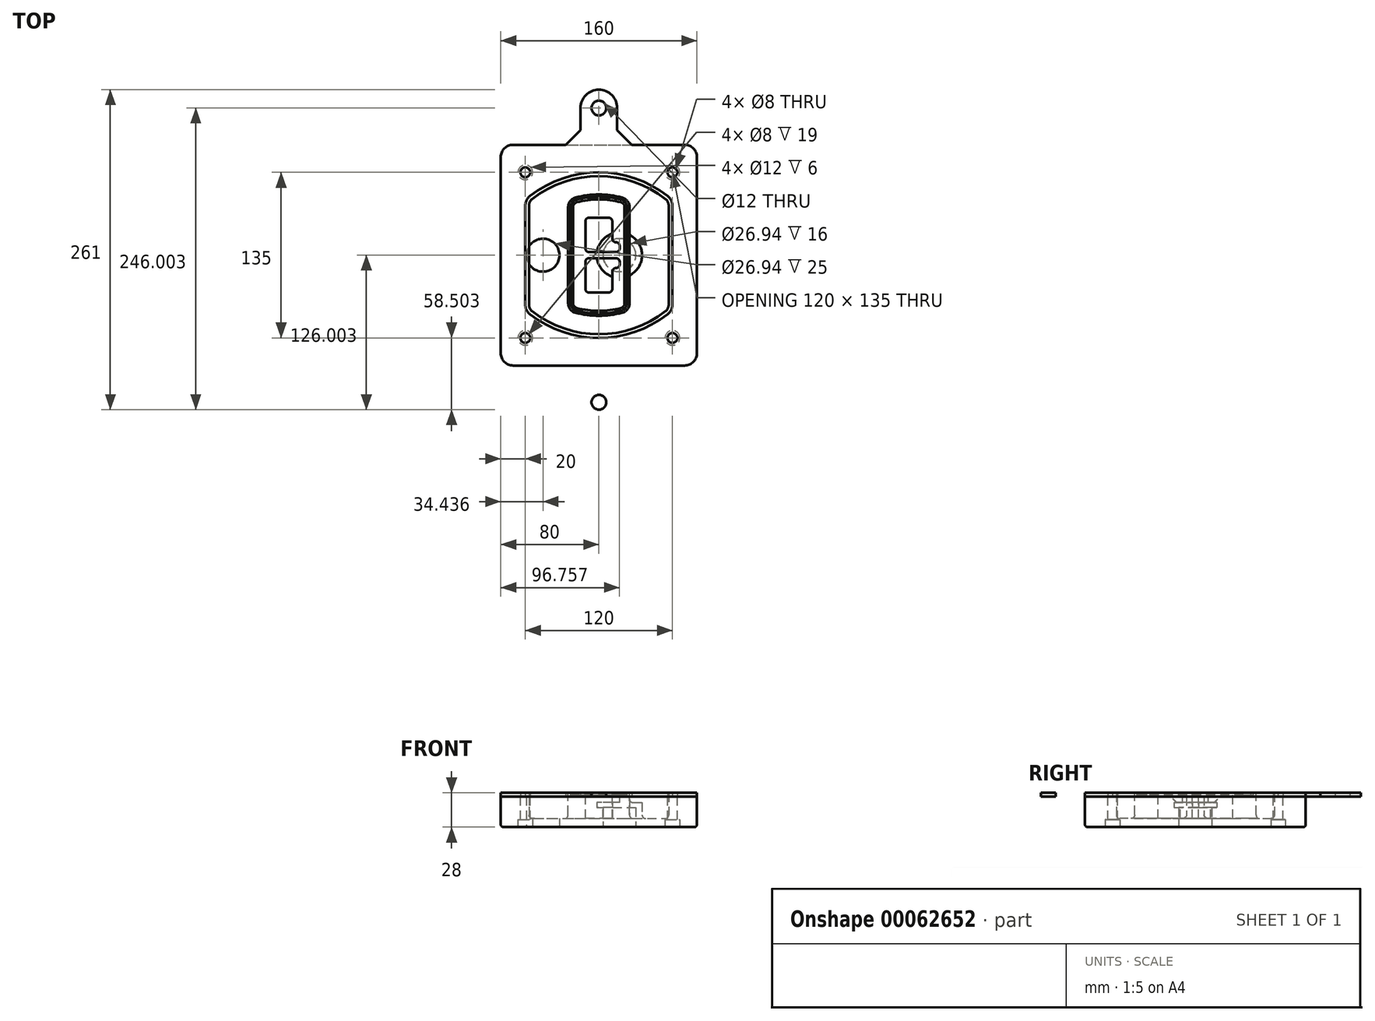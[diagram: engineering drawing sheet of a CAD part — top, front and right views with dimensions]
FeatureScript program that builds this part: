
annotation { "Feature Type Name" : "Feature", "Feature Type Description" : "" }
export const myFeature = defineFeature(function(context is Context, id is Id, definition is map)
    precondition{}
    {
        {
            var Q0;
            Q0=qCreatedBy(makeId("Top.planeOp"),FACE);
            var sketch = newSketch(context, id + "F0", { "sketchPlane" : qUnion([Q0])});
            skPoint(sketch, "E0.rect.middle", {"position": v(0, 0) * mm});
            skLineSegment(sketch, "E1.bottom", {"start": v(24.05, 28.38) * mm, "end": v(164.05, 28.38) * mm});
            skLineSegment(sketch, "E1.top", {"start": v(24.05, 208.38) * mm, "end": v(164.05, 208.38) * mm});
            skLineSegment(sketch, "E1.left", {"start": v(14.05, 38.38) * mm, "end": v(14.05, 198.38) * mm});
            skLineSegment(sketch, "E1.right", {"start": v(174.05, 38.38) * mm, "end": v(174.05, 198.38) * mm});
            skLineSegment(sketch, "E2", {"start": v(14.05, 208.38) * mm, "end": v(174.05, 28.38) * mm, "construction": true});
            skLineSegment(sketch, "E3", {"start": v(174.05, 208.38) * mm, "end": v(14.05, 28.38) * mm, "construction": true});
            skCircle(sketch, "E4", {"center": v(34.05, 185.88) * mm, "radius": 4 * mm});
            skCircle(sketch, "E5", {"center": v(154.05, 185.88) * mm, "radius": 4 * mm});
            skCircle(sketch, "E6", {"center": v(154.05, 50.88) * mm, "radius": 4 * mm});
            skCircle(sketch, "E7", {"center": v(34.05, 50.88) * mm, "radius": 4 * mm});
            skLineSegment(sketch, "E8", {"start": v(34.05, 185.88) * mm, "end": v(154.05, 185.88) * mm, "construction": true});
            skLineSegment(sketch, "E9", {"start": v(154.05, 185.88) * mm, "end": v(154.05, 50.88) * mm, "construction": true});
            skLineSegment(sketch, "E10", {"start": v(154.05, 50.88) * mm, "end": v(34.05, 50.88) * mm, "construction": true});
            skLineSegment(sketch, "E11", {"start": v(34.05, 50.88) * mm, "end": v(34.05, 185.88) * mm, "construction": true});
            skLineSegment(sketch, "E12", {"start": v(34.05, 158.68) * mm, "end": v(34.05, 78.09) * mm});
            skLineSegment(sketch, "E13", {"start": v(154.05, 158.68) * mm, "end": v(154.05, 78.09) * mm});
            skArc(sketch, "E14", {"start": v(150.2, 166.56) * mm, "mid": v(94.05, 185.88) * mm, "end": v(37.9, 166.56) * mm});
            skArc(sketch, "E15", {"start": v(37.9, 70.2) * mm, "mid": v(94.05, 50.88) * mm, "end": v(150.2, 70.2) * mm});
            skLineSegment(sketch, "E16", {"start": v(34.05, 118.38) * mm, "end": v(154.05, 118.38) * mm, "construction": true});
            skPoint(sketch, "E17.visualSharp", {"position": v(34.05, 73.38) * mm});
            skArc(sketch, "E17.filletArc", {"start": v(34.05, 78.09) * mm, "mid": v(35.06, 73.7) * mm, "end": v(37.9, 70.2) * mm});
            skPoint(sketch, "E18.visualSharp", {"position": v(34.05, 163.38) * mm});
            skArc(sketch, "E18.filletArc", {"start": v(37.9, 166.56) * mm, "mid": v(35.06, 163.06) * mm, "end": v(34.05, 158.68) * mm});
            skPoint(sketch, "E19.visualSharp", {"position": v(154.05, 163.38) * mm});
            skArc(sketch, "E19.filletArc", {"start": v(154.05, 158.68) * mm, "mid": v(153.04, 163.06) * mm, "end": v(150.2, 166.56) * mm});
            skPoint(sketch, "E20.visualSharp", {"position": v(154.05, 73.38) * mm});
            skArc(sketch, "E20.filletArc", {"start": v(150.2, 70.2) * mm, "mid": v(153.04, 73.7) * mm, "end": v(154.05, 78.09) * mm});
            skPoint(sketch, "E21.visualSharp", {"position": v(14.05, 208.38) * mm});
            skArc(sketch, "E21.filletArc", {"start": v(24.05, 208.38) * mm, "mid": v(16.98, 205.45) * mm, "end": v(14.05, 198.38) * mm});
            skPoint(sketch, "E22.visualSharp", {"position": v(174.05, 208.38) * mm});
            skArc(sketch, "E22.filletArc", {"start": v(174.05, 198.38) * mm, "mid": v(171.12, 205.45) * mm, "end": v(164.05, 208.38) * mm});
            skPoint(sketch, "E23.visualSharp", {"position": v(174.05, 28.38) * mm});
            skArc(sketch, "E23.filletArc", {"start": v(164.05, 28.38) * mm, "mid": v(171.12, 31.31) * mm, "end": v(174.05, 38.38) * mm});
            skPoint(sketch, "E24.visualSharp", {"position": v(14.05, 28.38) * mm});
            skArc(sketch, "E24.filletArc", {"start": v(14.05, 38.38) * mm, "mid": v(16.98, 31.31) * mm, "end": v(24.05, 28.38) * mm});
            skArc(sketch, "E25.0", {"start": v(151.05, 158.68) * mm, "mid": v(150.34, 161.75) * mm, "end": v(148.36, 164.2) * mm});
            skLineSegment(sketch, "E25.1", {"start": v(151.05, 158.68) * mm, "end": v(151.05, 78.09) * mm});
            skArc(sketch, "E25.2", {"start": v(148.36, 72.57) * mm, "mid": v(150.34, 75.02) * mm, "end": v(151.05, 78.09) * mm});
            skArc(sketch, "E25.3", {"start": v(39.74, 72.57) * mm, "mid": v(94.05, 53.88) * mm, "end": v(148.36, 72.57) * mm});
            skArc(sketch, "E25.4", {"start": v(37.05, 78.09) * mm, "mid": v(37.76, 75.02) * mm, "end": v(39.74, 72.57) * mm});
            skArc(sketch, "E25.5", {"start": v(148.36, 164.2) * mm, "mid": v(94.05, 182.88) * mm, "end": v(39.74, 164.2) * mm});
            skLineSegment(sketch, "E25.6", {"start": v(37.05, 158.68) * mm, "end": v(37.05, 78.09) * mm});
            skArc(sketch, "E25.7", {"start": v(39.74, 164.2) * mm, "mid": v(37.76, 161.75) * mm, "end": v(37.05, 158.68) * mm});
            skArc(sketch, "E26.0", {"start": v(35.43, 169.71) * mm, "mid": v(31.47, 164.82) * mm, "end": v(30.05, 158.68) * mm});
            skArc(sketch, "E26.1", {"start": v(152.67, 169.71) * mm, "mid": v(94.05, 189.88) * mm, "end": v(35.43, 169.71) * mm});
            skArc(sketch, "E26.2", {"start": v(158.05, 158.68) * mm, "mid": v(156.63, 164.82) * mm, "end": v(152.67, 169.71) * mm});
            skLineSegment(sketch, "E26.3", {"start": v(158.05, 158.68) * mm, "end": v(158.05, 78.09) * mm});
            skArc(sketch, "E26.4", {"start": v(152.67, 67.05) * mm, "mid": v(156.63, 71.95) * mm, "end": v(158.05, 78.09) * mm});
            skLineSegment(sketch, "E26.5", {"start": v(30.05, 158.68) * mm, "end": v(30.05, 78.09) * mm});
            skArc(sketch, "E26.6", {"start": v(35.43, 67.05) * mm, "mid": v(94.05, 46.88) * mm, "end": v(152.67, 67.05) * mm});
            skArc(sketch, "E26.7", {"start": v(30.05, 78.09) * mm, "mid": v(31.47, 71.95) * mm, "end": v(35.43, 67.05) * mm});
            skSolve(sketch);
        }
        {
            var Q0;
            Q0=makeQuery(id+"F0.imprint","IMPRINT",FACE,{"disambiguationData":[TD([[makeQuery(id+"F0.imprint","IMPRINT",EDGE,{"derivedFrom":sQuery(id+"F0.wireOp",EDGE,"E1.bottom")}),1.0]])]});
            var Q1;
            Q1=makeQuery(id+"F0.imprint","IMPRINT",FACE,{"disambiguationData":[TD([[makeQuery(id+"F0.imprint","IMPRINT",EDGE,{"derivedFrom":sQuery(id+"F0.wireOp",EDGE,"E12")}),1.0]])]});
            var Q2;
            Q2=makeQuery(id+"F0.imprint","IMPRINT",FACE,{"disambiguationData":[TD([[makeQuery(id+"F0.imprint","IMPRINT",EDGE,{"derivedFrom":sQuery(id+"F0.wireOp",EDGE,"E25.0")}),1.0]])]});
            var Q3;
            Q3=makeQuery(id+"F0.imprint","IMPRINT",FACE,{"disambiguationData":[TD([[makeQuery(id+"F0.imprint","IMPRINT",EDGE,{"derivedFrom":sQuery(id+"F0.wireOp",EDGE,"E12")}),-1.0]])]});
            extrude(context, id + "F1", {"entities" : qUnion([Q0, Q1, Q2, Q3]), "oppositeDirection" : true, "depth" : 25 * mm});
        }
        {
            var Q0;
            Q0=makeQuery(id+"F0.imprint","IMPRINT",FACE,{"disambiguationData":[TD([[makeQuery(id+"F0.imprint","IMPRINT",EDGE,{"derivedFrom":sQuery(id+"F0.wireOp",EDGE,"E12")}),1.0]])]});
            extrude(context, id + "F2", {"entities" : qUnion([Q0]), "operationType" : NewBodyOperationType.ADD, "depth" : 3 * mm});
        }
        {
            var Q0;
            Q0=makeQuery(id+"F0.imprint","IMPRINT",FACE,{"disambiguationData":[TD([[makeQuery(id+"F0.imprint","IMPRINT",EDGE,{"derivedFrom":sQuery(id+"F0.wireOp",EDGE,"E25.0")}),1.0]])]});
            extrude(context, id + "F3", {"entities" : qUnion([Q0]), "operationType" : NewBodyOperationType.REMOVE, "oppositeDirection" : true, "depth" : 18 * mm});
        }
        {
            var Q0;
            Q0=makeQuery(id+"F2.opExtrude","CAP_FACE",FACE,{"disambiguationData":[OSD([sQuery(id+"F0.wireOp",EDGE,"E12"),sQuery(id+"F0.wireOp",EDGE,"E13"),sQuery(id+"F0.wireOp",EDGE,"E14"),sQuery(id+"F0.wireOp",EDGE,"E15"),sQuery(id+"F0.wireOp",EDGE,"E17.filletArc"),sQuery(id+"F0.wireOp",EDGE,"E18.filletArc"),sQuery(id+"F0.wireOp",EDGE,"E19.filletArc"),sQuery(id+"F0.wireOp",EDGE,"E20.filletArc"),sQuery(id+"F0.wireOp",EDGE,"E25.0"),sQuery(id+"F0.wireOp",EDGE,"E25.1"),sQuery(id+"F0.wireOp",EDGE,"E25.2"),sQuery(id+"F0.wireOp",EDGE,"E25.3"),sQuery(id+"F0.wireOp",EDGE,"E25.4"),sQuery(id+"F0.wireOp",EDGE,"E25.5"),sQuery(id+"F0.wireOp",EDGE,"E25.6"),sQuery(id+"F0.wireOp",EDGE,"E25.7")])],"isStart":false});
            var sketch = newSketch(context, id + "F4", { "sketchPlane" : qUnion([Q0])});
            skArc(sketch, "E27.0", {"start": v(74.97, 71.41) * mm, "mid": v(94.05, 68.88) * mm, "end": v(113.13, 71.41) * mm});
            skArc(sketch, "E28.0", {"start": v(113.13, 165.35) * mm, "mid": v(94.05, 167.88) * mm, "end": v(74.97, 165.35) * mm});
            skLineSegment(sketch, "E29", {"start": v(69.05, 157.63) * mm, "end": v(69.05, 79.14) * mm});
            skLineSegment(sketch, "E30", {"start": v(119.05, 157.63) * mm, "end": v(119.05, 79.14) * mm});
            skLineSegment(sketch, "E31", {"start": v(69.05, 163.48) * mm, "end": v(119.05, 163.48) * mm, "construction": true});
            skLineSegment(sketch, "E32", {"start": v(69.05, 73.28) * mm, "end": v(119.05, 73.28) * mm, "construction": true});
            skPoint(sketch, "E33.visualSharp", {"position": v(69.05, 163.48) * mm});
            skArc(sketch, "E33.filletArc", {"start": v(74.97, 165.35) * mm, "mid": v(70.7, 162.5) * mm, "end": v(69.05, 157.63) * mm});
            skPoint(sketch, "E34.visualSharp", {"position": v(119.05, 163.48) * mm});
            skArc(sketch, "E34.filletArc", {"start": v(119.05, 157.63) * mm, "mid": v(117.4, 162.5) * mm, "end": v(113.13, 165.35) * mm});
            skPoint(sketch, "E35.visualSharp", {"position": v(119.05, 73.28) * mm});
            skArc(sketch, "E35.filletArc", {"start": v(113.13, 71.41) * mm, "mid": v(117.4, 74.27) * mm, "end": v(119.05, 79.14) * mm});
            skPoint(sketch, "E36.visualSharp", {"position": v(69.05, 73.28) * mm});
            skArc(sketch, "E36.filletArc", {"start": v(69.05, 79.14) * mm, "mid": v(70.7, 74.27) * mm, "end": v(74.97, 71.41) * mm});
            skArc(sketch, "E37.0", {"start": v(148.36, 164.2) * mm, "mid": v(94.05, 182.88) * mm, "end": v(39.74, 164.2) * mm});
            skArc(sketch, "E37.1", {"start": v(39.74, 164.2) * mm, "mid": v(37.76, 161.75) * mm, "end": v(37.05, 158.68) * mm});
            skLineSegment(sketch, "E37.2", {"start": v(37.05, 158.68) * mm, "end": v(37.05, 78.09) * mm});
            skArc(sketch, "E37.3", {"start": v(37.05, 78.09) * mm, "mid": v(37.76, 75.02) * mm, "end": v(39.74, 72.57) * mm});
            skArc(sketch, "E37.4", {"start": v(39.74, 72.57) * mm, "mid": v(94.05, 53.88) * mm, "end": v(148.36, 72.57) * mm});
            skArc(sketch, "E37.5", {"start": v(148.36, 72.57) * mm, "mid": v(150.34, 75.02) * mm, "end": v(151.05, 78.09) * mm});
            skLineSegment(sketch, "E37.6", {"start": v(151.05, 158.68) * mm, "end": v(151.05, 78.09) * mm});
            skArc(sketch, "E37.7", {"start": v(151.05, 158.68) * mm, "mid": v(150.34, 161.75) * mm, "end": v(148.36, 164.2) * mm});
            skLineSegment(sketch, "E38.0", {"start": v(117.05, 157.63) * mm, "end": v(117.05, 79.14) * mm});
            skArc(sketch, "E38.1", {"start": v(112.61, 73.34) * mm, "mid": v(115.81, 75.49) * mm, "end": v(117.05, 79.14) * mm});
            skArc(sketch, "E38.2", {"start": v(75.49, 73.34) * mm, "mid": v(94.05, 70.88) * mm, "end": v(112.61, 73.34) * mm});
            skArc(sketch, "E38.3", {"start": v(71.05, 79.14) * mm, "mid": v(72.29, 75.49) * mm, "end": v(75.49, 73.34) * mm});
            skLineSegment(sketch, "E38.4", {"start": v(71.05, 157.63) * mm, "end": v(71.05, 79.14) * mm});
            skArc(sketch, "E38.5", {"start": v(117.05, 157.63) * mm, "mid": v(115.81, 161.28) * mm, "end": v(112.61, 163.42) * mm});
            skArc(sketch, "E38.6", {"start": v(75.49, 163.42) * mm, "mid": v(72.29, 161.28) * mm, "end": v(71.05, 157.63) * mm});
            skArc(sketch, "E38.7", {"start": v(112.61, 163.42) * mm, "mid": v(94.05, 165.88) * mm, "end": v(75.49, 163.42) * mm});
            skArc(sketch, "E39.0", {"start": v(115.05, 157.63) * mm, "mid": v(114.23, 160.06) * mm, "end": v(112.1, 161.5) * mm});
            skLineSegment(sketch, "E39.1", {"start": v(115.05, 157.63) * mm, "end": v(115.05, 79.14) * mm});
            skArc(sketch, "E39.2", {"start": v(112.1, 75.27) * mm, "mid": v(114.23, 76.7) * mm, "end": v(115.05, 79.14) * mm});
            skArc(sketch, "E39.3", {"start": v(76, 75.27) * mm, "mid": v(94.05, 72.88) * mm, "end": v(112.1, 75.27) * mm});
            skArc(sketch, "E39.4", {"start": v(73.05, 79.14) * mm, "mid": v(73.87, 76.7) * mm, "end": v(76, 75.27) * mm});
            skArc(sketch, "E39.5", {"start": v(112.1, 161.5) * mm, "mid": v(94.05, 163.88) * mm, "end": v(76, 161.5) * mm});
            skLineSegment(sketch, "E39.6", {"start": v(73.05, 157.63) * mm, "end": v(73.05, 79.14) * mm});
            skArc(sketch, "E39.7", {"start": v(76, 161.5) * mm, "mid": v(73.87, 160.06) * mm, "end": v(73.05, 157.63) * mm});
            skLineSegment(sketch, "E40", {"start": v(69.05, 118.38) * mm, "end": v(119.05, 118.38) * mm, "construction": true});
            skLineSegment(sketch, "E41", {"start": v(83.05, 123.88) * mm, "end": v(83.05, 145.88) * mm});
            skLineSegment(sketch, "E42", {"start": v(86.05, 148.88) * mm, "end": v(102.05, 148.88) * mm});
            skLineSegment(sketch, "E43", {"start": v(105.05, 145.88) * mm, "end": v(105.05, 131.88) * mm});
            skLineSegment(sketch, "E44", {"start": v(108.05, 128.88) * mm, "end": v(108.05, 128.88) * mm});
            skLineSegment(sketch, "E45", {"start": v(111.05, 125.88) * mm, "end": v(111.05, 123.88) * mm});
            skLineSegment(sketch, "E46", {"start": v(108.05, 120.88) * mm, "end": v(86.05, 120.88) * mm});
            skPoint(sketch, "E47.visualSharp", {"position": v(83.05, 148.88) * mm});
            skArc(sketch, "E47.filletArc", {"start": v(86.05, 148.88) * mm, "mid": v(83.93, 148) * mm, "end": v(83.05, 145.88) * mm});
            skPoint(sketch, "E48.visualSharp", {"position": v(105.05, 148.88) * mm});
            skArc(sketch, "E48.filletArc", {"start": v(105.05, 145.88) * mm, "mid": v(104.17, 148) * mm, "end": v(102.05, 148.88) * mm});
            skPoint(sketch, "E49.visualSharp", {"position": v(105.05, 128.88) * mm});
            skArc(sketch, "E49.filletArc", {"start": v(105.05, 131.88) * mm, "mid": v(105.93, 129.76) * mm, "end": v(108.05, 128.88) * mm});
            skPoint(sketch, "E50.visualSharp", {"position": v(111.05, 128.88) * mm});
            skArc(sketch, "E50.filletArc", {"start": v(111.05, 125.88) * mm, "mid": v(110.17, 128) * mm, "end": v(108.05, 128.88) * mm});
            skPoint(sketch, "E51.visualSharp", {"position": v(111.05, 120.88) * mm});
            skArc(sketch, "E51.filletArc", {"start": v(108.05, 120.88) * mm, "mid": v(110.17, 121.76) * mm, "end": v(111.05, 123.88) * mm});
            skPoint(sketch, "E52.visualSharp", {"position": v(83.05, 120.88) * mm});
            skArc(sketch, "E52.filletArc", {"start": v(83.05, 123.88) * mm, "mid": v(83.93, 121.76) * mm, "end": v(86.05, 120.88) * mm});
            skLineSegment(sketch, "E53.0.MirrorCS", {"start": v(108.05, 115.88) * mm, "end": v(86.05, 115.88) * mm});
            skArc(sketch, "E54.0.MirrorCS", {"start": v(83.05, 112.88) * mm, "mid": v(83.93, 115) * mm, "end": v(86.05, 115.88) * mm});
            skLineSegment(sketch, "E55.0.MirrorCS", {"start": v(83.05, 112.88) * mm, "end": v(83.05, 90.88) * mm});
            skArc(sketch, "E56.0.MirrorCS", {"start": v(86.05, 87.88) * mm, "mid": v(83.93, 88.76) * mm, "end": v(83.05, 90.88) * mm});
            skLineSegment(sketch, "E57.0.MirrorCS", {"start": v(86.05, 87.88) * mm, "end": v(102.05, 87.88) * mm});
            skArc(sketch, "E58.0.MirrorCS", {"start": v(105.05, 90.88) * mm, "mid": v(104.17, 88.76) * mm, "end": v(102.05, 87.88) * mm});
            skLineSegment(sketch, "E59.0.MirrorCS", {"start": v(105.05, 90.88) * mm, "end": v(105.05, 104.88) * mm});
            skArc(sketch, "E60.0.MirrorCS", {"start": v(105.05, 104.88) * mm, "mid": v(105.93, 107) * mm, "end": v(108.05, 107.88) * mm});
            skArc(sketch, "E61.0.MirrorCS", {"start": v(111.05, 110.88) * mm, "mid": v(110.17, 108.76) * mm, "end": v(108.05, 107.88) * mm});
            skLineSegment(sketch, "E62.0.MirrorCS", {"start": v(111.05, 110.88) * mm, "end": v(111.05, 112.88) * mm});
            skArc(sketch, "E63.0.MirrorCS", {"start": v(108.05, 115.88) * mm, "mid": v(110.17, 115) * mm, "end": v(111.05, 112.88) * mm});
            skSolve(sketch);
        }
        {
            var Q0;
            Q0=makeQuery(id+"F4.imprint","IMPRINT",FACE,{"disambiguationData":[TD([[makeQuery(id+"F4.imprint","IMPRINT",EDGE,{"derivedFrom":sQuery(id+"F4.wireOp",EDGE,"E27.0")}),1.0]])]});
            var Q1;
            Q1=makeQuery(id+"F4.imprint","IMPRINT",FACE,{"disambiguationData":[TD([[makeQuery(id+"F4.imprint","IMPRINT",EDGE,{"derivedFrom":sQuery(id+"F4.wireOp",EDGE,"E38.0")}),-1.0]])]});
            var Q2;
            Q2=makeQuery(id+"F4.imprint","IMPRINT",FACE,{"disambiguationData":[TD([[makeQuery(id+"F4.imprint","IMPRINT",EDGE,{"derivedFrom":sQuery(id+"F4.wireOp",EDGE,"E39.0")}),1.0]])]});
            extrude(context, id + "F5", {"entities" : qUnion([Q0, Q1, Q2]), "operationType" : NewBodyOperationType.ADD, "endBound" : BoundingType.UP_TO_NEXT, "oppositeDirection" : true, "depth" : 25 * mm});
        }
        {
            var Q0;
            Q0=makeQuery(id+"F4.imprint","IMPRINT",FACE,{"disambiguationData":[TD([[makeQuery(id+"F4.imprint","IMPRINT",EDGE,{"derivedFrom":sQuery(id+"F4.wireOp",EDGE,"E38.0")}),-1.0]])]});
            extrude(context, id + "F6", {"entities" : qUnion([Q0]), "operationType" : NewBodyOperationType.REMOVE, "oppositeDirection" : true, "depth" : 2 * mm});
        }
        {
            var Q0;
            Q0=makeQuery(id+"F1.opExtrude","CAP_FACE",FACE,{"disambiguationData":[OSD([sQuery(id+"F0.wireOp",EDGE,"E1.bottom"),sQuery(id+"F0.wireOp",EDGE,"E1.top"),sQuery(id+"F0.wireOp",EDGE,"E1.left"),sQuery(id+"F0.wireOp",EDGE,"E1.right"),sQuery(id+"F0.wireOp",EDGE,"E4"),sQuery(id+"F0.wireOp",EDGE,"E5"),sQuery(id+"F0.wireOp",EDGE,"E6"),sQuery(id+"F0.wireOp",EDGE,"E7"),sQuery(id+"F0.wireOp",EDGE,"E21.filletArc"),sQuery(id+"F0.wireOp",EDGE,"E22.filletArc"),sQuery(id+"F0.wireOp",EDGE,"E23.filletArc"),sQuery(id+"F0.wireOp",EDGE,"E24.filletArc")])],"isStart":false});
            var sketch = newSketch(context, id + "F7", { "sketchPlane" : qUnion([Q0])});
            skCircle(sketch, "E64", {"center": v(110.8, -118.38) * mm, "radius": 13.47 * mm});
            skCircle(sketch, "E65", {"center": v(48.49, -118.38) * mm, "radius": 13.47 * mm});
            skLineSegment(sketch, "E66", {"start": v(174.05, -118.38) * mm, "end": v(14.05, -118.38) * mm});
            skCircle(sketch, "E67", {"center": v(110.8, -118.38) * mm, "radius": 18.47 * mm});
            skCircle(sketch, "E68", {"center": v(154.05, -185.88) * mm, "radius": 6 * mm});
            skCircle(sketch, "E69", {"center": v(34.05, -185.88) * mm, "radius": 6 * mm});
            skCircle(sketch, "E70", {"center": v(34.05, -50.88) * mm, "radius": 6 * mm});
            skCircle(sketch, "E71", {"center": v(154.05, -50.88) * mm, "radius": 6 * mm});
            skSolve(sketch);
        }
        {
            var Q0;
            {var subQ1=sQuery(id+"F7.wireOp",EDGE,"E66");var subQ4=sQuery(id+"F7.wireOp",EDGE,"E64");var subQ6=makeQuery(id+"F7.imprint","INTERSECT",VERTEX,{"disambiguationData":[OD(0.0)],"derivedFrom":[subQ4,subQ1]});Q0=makeQuery(id+"F7.imprint","IMPRINT",FACE,{"disambiguationData":[TD([[makeQuery(id+"F7.imprint","IMPRINT",EDGE,{"disambiguationData":[TD([[subQ6,-1.0]])],"derivedFrom":subQ4}),-1.0]])]});}
            var Q1;
            {var subQ0=sQuery(id+"F7.wireOp",EDGE,"E66");var subQ1=sQuery(id+"F7.wireOp",EDGE,"E64");var subQ3=makeQuery(id+"F7.imprint","INTERSECT",VERTEX,{"disambiguationData":[OD(0.0)],"derivedFrom":[subQ1,subQ0]});Q1=makeQuery(id+"F7.imprint","IMPRINT",FACE,{"disambiguationData":[TD([[makeQuery(id+"F7.imprint","IMPRINT",EDGE,{"disambiguationData":[TD([[subQ3,-1.0]])],"derivedFrom":subQ1}),1.0]])]});}
            var Q2;
            {var subQ0=sQuery(id+"F7.wireOp",EDGE,"E66");var subQ1=sQuery(id+"F7.wireOp",EDGE,"E64");var subQ3=makeQuery(id+"F7.imprint","INTERSECT",VERTEX,{"disambiguationData":[OD(0.0)],"derivedFrom":[subQ1,subQ0]});Q2=makeQuery(id+"F7.imprint","IMPRINT",FACE,{"disambiguationData":[TD([[makeQuery(id+"F7.imprint","IMPRINT",EDGE,{"disambiguationData":[TD([[subQ3,1.0]])],"derivedFrom":subQ1}),1.0]])]});}
            var Q3;
            {var subQ1=sQuery(id+"F7.wireOp",EDGE,"E66");var subQ4=sQuery(id+"F7.wireOp",EDGE,"E64");var subQ6=makeQuery(id+"F7.imprint","INTERSECT",VERTEX,{"disambiguationData":[OD(0.0)],"derivedFrom":[subQ4,subQ1]});Q3=makeQuery(id+"F7.imprint","IMPRINT",FACE,{"disambiguationData":[TD([[makeQuery(id+"F7.imprint","IMPRINT",EDGE,{"disambiguationData":[TD([[subQ6,1.0]])],"derivedFrom":subQ4}),-1.0]])]});}
            extrude(context, id + "F8", {"entities" : qUnion([Q0, Q1, Q2, Q3]), "operationType" : NewBodyOperationType.ADD, "oppositeDirection" : true, "depth" : 20 * mm});
        }
        {
            var Q0;
            {var subQ0=sQuery(id+"F7.wireOp",EDGE,"E66");var subQ1=sQuery(id+"F7.wireOp",EDGE,"E64");var subQ3=makeQuery(id+"F7.imprint","INTERSECT",VERTEX,{"disambiguationData":[OD(0.0)],"derivedFrom":[subQ1,subQ0]});Q0=makeQuery(id+"F7.imprint","IMPRINT",FACE,{"disambiguationData":[TD([[makeQuery(id+"F7.imprint","IMPRINT",EDGE,{"disambiguationData":[TD([[subQ3,-1.0]])],"derivedFrom":subQ1}),1.0]])]});}
            var Q1;
            {var subQ0=sQuery(id+"F7.wireOp",EDGE,"E66");var subQ1=sQuery(id+"F7.wireOp",EDGE,"E64");var subQ3=makeQuery(id+"F7.imprint","INTERSECT",VERTEX,{"disambiguationData":[OD(0.0)],"derivedFrom":[subQ1,subQ0]});Q1=makeQuery(id+"F7.imprint","IMPRINT",FACE,{"disambiguationData":[TD([[makeQuery(id+"F7.imprint","IMPRINT",EDGE,{"disambiguationData":[TD([[subQ3,1.0]])],"derivedFrom":subQ1}),1.0]])]});}
            extrude(context, id + "F9", {"entities" : qUnion([Q0, Q1]), "operationType" : NewBodyOperationType.REMOVE, "oppositeDirection" : true, "depth" : 16 * mm});
        }
        {
            var Q0;
            {var subQ0=sQuery(id+"F7.wireOp",EDGE,"E66");var subQ1=sQuery(id+"F7.wireOp",EDGE,"E65");var subQ3=makeQuery(id+"F7.imprint","INTERSECT",VERTEX,{"disambiguationData":[OD(0.0)],"derivedFrom":[subQ1,subQ0]});Q0=makeQuery(id+"F7.imprint","IMPRINT",FACE,{"disambiguationData":[TD([[makeQuery(id+"F7.imprint","IMPRINT",EDGE,{"disambiguationData":[TD([[subQ3,-1.0]])],"derivedFrom":subQ1}),1.0]])]});}
            var Q1;
            {var subQ0=sQuery(id+"F7.wireOp",EDGE,"E66");var subQ1=sQuery(id+"F7.wireOp",EDGE,"E65");var subQ3=makeQuery(id+"F7.imprint","INTERSECT",VERTEX,{"disambiguationData":[OD(0.0)],"derivedFrom":[subQ1,subQ0]});Q1=makeQuery(id+"F7.imprint","IMPRINT",FACE,{"disambiguationData":[TD([[makeQuery(id+"F7.imprint","IMPRINT",EDGE,{"disambiguationData":[TD([[subQ3,1.0]])],"derivedFrom":subQ1}),1.0]])]});}
            extrude(context, id + "F10", {"entities" : qUnion([Q0, Q1]), "operationType" : NewBodyOperationType.REMOVE, "oppositeDirection" : true, "depth" : 25 * mm});
        }
        {
            var Q0;
            Q0=makeQuery(id+"F7.imprint","IMPRINT",FACE,{"disambiguationData":[TD([[makeQuery(id+"F7.imprint","IMPRINT",EDGE,{"derivedFrom":sQuery(id+"F7.wireOp",EDGE,"E68")}),1.0]])]});
            var Q1;
            Q1=makeQuery(id+"F7.imprint","IMPRINT",FACE,{"disambiguationData":[TD([[makeQuery(id+"F7.imprint","IMPRINT",EDGE,{"derivedFrom":makeQuery(id+"F1.opExtrude","CAP_EDGE",EDGE,{"disambiguationData":[OSD([sQuery(id+"F0.wireOp",EDGE,"E5")])],"isStart":false})}),-1.0]])]});
            var Q2;
            Q2=makeQuery(id+"F7.imprint","IMPRINT",FACE,{"disambiguationData":[TD([[makeQuery(id+"F7.imprint","IMPRINT",EDGE,{"derivedFrom":sQuery(id+"F7.wireOp",EDGE,"E69")}),1.0]])]});
            var Q3;
            Q3=makeQuery(id+"F7.imprint","IMPRINT",FACE,{"disambiguationData":[TD([[makeQuery(id+"F7.imprint","IMPRINT",EDGE,{"derivedFrom":makeQuery(id+"F1.opExtrude","CAP_EDGE",EDGE,{"disambiguationData":[OSD([sQuery(id+"F0.wireOp",EDGE,"E4")])],"isStart":false})}),-1.0]])]});
            var Q4;
            Q4=makeQuery(id+"F7.imprint","IMPRINT",FACE,{"disambiguationData":[TD([[makeQuery(id+"F7.imprint","IMPRINT",EDGE,{"derivedFrom":sQuery(id+"F7.wireOp",EDGE,"E70")}),1.0]])]});
            var Q5;
            Q5=makeQuery(id+"F7.imprint","IMPRINT",FACE,{"disambiguationData":[TD([[makeQuery(id+"F7.imprint","IMPRINT",EDGE,{"derivedFrom":makeQuery(id+"F1.opExtrude","CAP_EDGE",EDGE,{"disambiguationData":[OSD([sQuery(id+"F0.wireOp",EDGE,"E7")])],"isStart":false})}),-1.0]])]});
            var Q6;
            Q6=makeQuery(id+"F7.imprint","IMPRINT",FACE,{"disambiguationData":[TD([[makeQuery(id+"F7.imprint","IMPRINT",EDGE,{"derivedFrom":sQuery(id+"F7.wireOp",EDGE,"E71")}),1.0]])]});
            var Q7;
            Q7=makeQuery(id+"F7.imprint","IMPRINT",FACE,{"disambiguationData":[TD([[makeQuery(id+"F7.imprint","IMPRINT",EDGE,{"derivedFrom":makeQuery(id+"F1.opExtrude","CAP_EDGE",EDGE,{"disambiguationData":[OSD([sQuery(id+"F0.wireOp",EDGE,"E6")])],"isStart":false})}),-1.0]])]});
            extrude(context, id + "F11", {"entities" : qUnion([Q0, Q1, Q2, Q3, Q4, Q5, Q6, Q7]), "operationType" : NewBodyOperationType.REMOVE, "oppositeDirection" : true, "depth" : 6 * mm});
        }
        {
            var Q0;
            Q0=makeQuery(id+"F9.boolean.opBoolean","COPY",FACE,{"derivedFrom":makeQuery(id+"F9.opExtrude","CAP_FACE",FACE,{"disambiguationData":[OSD([sQuery(id+"F7.wireOp",EDGE,"E64")])],"isStart":false})});
            var sketch = newSketch(context, id + "F12", { "sketchPlane" : qUnion([Q0])});
            skArc(sketch, "E72.0", {"start": v(105.05, -100.83) * mm, "mid": v(96.62, -106.56) * mm, "end": v(92.5, -115.88) * mm});
            skArc(sketch, "E72.1", {"start": v(92.5, -120.88) * mm, "mid": v(96.62, -130.2) * mm, "end": v(105.05, -135.93) * mm});
            skLineSegment(sketch, "E73", {"start": v(92.5, -120.88) * mm, "end": v(108.05, -120.88) * mm});
            skLineSegment(sketch, "E74.0", {"start": v(108.05, -115.88) * mm, "end": v(92.5, -115.88) * mm});
            skArc(sketch, "E74.1", {"start": v(108.05, -115.88) * mm, "mid": v(110.17, -115) * mm, "end": v(111.05, -112.88) * mm});
            skLineSegment(sketch, "E74.2", {"start": v(111.05, -110.88) * mm, "end": v(111.05, -112.88) * mm});
            skArc(sketch, "E74.3", {"start": v(111.05, -110.88) * mm, "mid": v(110.17, -108.76) * mm, "end": v(108.05, -107.88) * mm});
            skArc(sketch, "E74.4", {"start": v(105.05, -104.88) * mm, "mid": v(105.93, -107) * mm, "end": v(108.05, -107.88) * mm});
            skLineSegment(sketch, "E74.5", {"start": v(105.05, -100.83) * mm, "end": v(105.05, -104.88) * mm});
            skLineSegment(sketch, "E74.7", {"start": v(108.05, -120.88) * mm, "end": v(92.5, -120.88) * mm});
            skArc(sketch, "E74.8", {"start": v(108.05, -120.88) * mm, "mid": v(110.17, -121.76) * mm, "end": v(111.05, -123.88) * mm});
            skLineSegment(sketch, "E74.9", {"start": v(111.05, -125.88) * mm, "end": v(111.05, -123.88) * mm});
            skArc(sketch, "E74.10", {"start": v(111.05, -125.88) * mm, "mid": v(110.17, -128) * mm, "end": v(108.05, -128.88) * mm});
            skArc(sketch, "E74.11", {"start": v(105.05, -131.88) * mm, "mid": v(105.93, -129.76) * mm, "end": v(108.05, -128.88) * mm});
            skLineSegment(sketch, "E74.12", {"start": v(105.05, -135.93) * mm, "end": v(105.05, -131.88) * mm});
            skPoint(sketch, "E75.orphan", {"position": v(105.05, -145.88) * mm});
            skPoint(sketch, "E76.orphan", {"position": v(86.05, -120.88) * mm});
            skPoint(sketch, "E77.orphan", {"position": v(86.05, -115.88) * mm});
            skPoint(sketch, "E78.orphan", {"position": v(105.05, -90.88) * mm});
            skSolve(sketch);
        }
        {
            var Q0;
            {var subQ7=sQuery(id+"F12.wireOp",EDGE,"E72.0");var subQ14=sQuery(id+"F12.wireOp",EDGE,"E72.1");var subQ16=sQuery(id+"F12.wireOp",EDGE,"E74.1");var subQ18=sQuery(id+"F12.wireOp",EDGE,"E74.8");Q0=qUnion([makeQuery(id+"F12.imprint","IMPRINT",FACE,{"disambiguationData":[TD([[makeQuery(id+"F12.imprint","IMPRINT",EDGE,{"derivedFrom":subQ7}),1.0]])]}),makeQuery(id+"F12.imprint","IMPRINT",FACE,{"disambiguationData":[TD([[makeQuery(id+"F12.imprint","IMPRINT",EDGE,{"derivedFrom":subQ14}),1.0]])]}),makeQuery(id+"F12.imprint","IMPRINT",FACE,{"disambiguationData":[TD([[makeQuery(id+"F12.imprint","IMPRINT",EDGE,{"derivedFrom":subQ16}),1.0]])]}),makeQuery(id+"F12.imprint","IMPRINT",FACE,{"disambiguationData":[TD([[makeQuery(id+"F12.imprint","IMPRINT",EDGE,{"derivedFrom":subQ18}),-1.0]])]})]);}
            var Q1;
            Q1=makeQuery(id+"F5.boolean.opBoolean","SPLIT",FACE,{"disambiguationData":[TD([makeQuery(id+"F5.opExtrude","SWEPT_FACE",FACE,{"disambiguationData":[OSD([sQuery(id+"F4.wireOp",EDGE,"E41")])]})])],"derivedFrom":makeQuery(id+"F3.boolean.opBoolean","COPY",FACE,{"derivedFrom":makeQuery(id+"F3.opExtrude","CAP_FACE",FACE,{"disambiguationData":[OSD([sQuery(id+"F0.wireOp",EDGE,"E25.0"),sQuery(id+"F0.wireOp",EDGE,"E25.1"),sQuery(id+"F0.wireOp",EDGE,"E25.2"),sQuery(id+"F0.wireOp",EDGE,"E25.3"),sQuery(id+"F0.wireOp",EDGE,"E25.4"),sQuery(id+"F0.wireOp",EDGE,"E25.5"),sQuery(id+"F0.wireOp",EDGE,"E25.6"),sQuery(id+"F0.wireOp",EDGE,"E25.7")])],"isStart":false})})});
            extrude(context, id + "F13", {"entities" : qUnion([Q0]), "operationType" : NewBodyOperationType.REMOVE, "endBound" : BoundingType.UP_TO_SURFACE, "endBoundEntityFace" : qUnion([Q1]), "depth" : 25 * mm});
        }
        {
            var Q0;
            Q0=makeQuery(id+"F3.boolean.opBoolean","COPY",EDGE,{"derivedFrom":makeQuery(id+"F3.opExtrude","CAP_EDGE",EDGE,{"disambiguationData":[OSD([sQuery(id+"F0.wireOp",EDGE,"E25.6")])],"isStart":false})});
            var Q1;
            Q1=makeQuery(id+"F8.boolean.opBoolean","INTERSECT",EDGE,{"derivedFrom":[makeQuery(id+"F5.opExtrude","SWEPT_FACE",FACE,{"disambiguationData":[OSD([sQuery(id+"F4.wireOp",EDGE,"E30")])]}),makeQuery(id+"F8.opExtrude","CAP_FACE",FACE,{"disambiguationData":[OSD([sQuery(id+"F7.wireOp",EDGE,"E67")])],"isStart":false})]});
            var Q2;
            Q2=makeQuery(id+"F8.boolean.opBoolean","INTERSECT",EDGE,{"disambiguationData":[OD(1.0)],"derivedFrom":[makeQuery(id+"F5.opExtrude","SWEPT_FACE",FACE,{"disambiguationData":[OSD([sQuery(id+"F4.wireOp",EDGE,"E30")])]}),makeQuery(id+"F8.opExtrude","SWEPT_FACE",FACE,{"disambiguationData":[OSD([sQuery(id+"F7.wireOp",EDGE,"E67")])]})]});
            var Q3;
            {var subQ0=sQuery(id+"F4.wireOp",EDGE,"E30");Q3=makeQuery(id+"F8.boolean.opBoolean","SPLIT",EDGE,{"disambiguationData":[TD([makeQuery(id+"F5.opExtrude","SWEPT_FACE",FACE,{"disambiguationData":[OSD([sQuery(id+"F4.wireOp",EDGE,"E35.filletArc")])]})])],"derivedFrom":makeQuery(id+"F5.opExtrude","CAP_EDGE",EDGE,{"disambiguationData":[OSD([subQ0])],"isStart":false})});}
            var Q4;
            {var subQ0=sQuery(id+"F0.wireOp",EDGE,"E25.7");var subQ1=sQuery(id+"F0.wireOp",EDGE,"E25.1");var subQ2=sQuery(id+"F0.wireOp",EDGE,"E25.6");var subQ3=sQuery(id+"F0.wireOp",EDGE,"E25.5");var subQ4=sQuery(id+"F0.wireOp",EDGE,"E25.4");var subQ5=sQuery(id+"F0.wireOp",EDGE,"E25.0");var subQ6=sQuery(id+"F0.wireOp",EDGE,"E25.2");var subQ7=sQuery(id+"F0.wireOp",EDGE,"E25.3");Q4=makeQuery(id+"F8.boolean.opBoolean","INTERSECT",EDGE,{"derivedFrom":[makeQuery(id+"F5.boolean.opBoolean","SPLIT",FACE,{"disambiguationData":[TD([makeQuery(id+"F2.opExtrude","SWEPT_FACE",FACE,{"disambiguationData":[OSD([subQ5])]})])],"derivedFrom":makeQuery(id+"F3.boolean.opBoolean","COPY",FACE,{"derivedFrom":makeQuery(id+"F3.opExtrude","CAP_FACE",FACE,{"disambiguationData":[OSD([subQ5,subQ1,subQ6,subQ7,subQ4,subQ3,subQ2,subQ0])],"isStart":false})})}),makeQuery(id+"F8.opExtrude","SWEPT_FACE",FACE,{"disambiguationData":[OSD([sQuery(id+"F7.wireOp",EDGE,"E67")])]})]});}
            var Q5;
            Q5=makeQuery(id+"F8.boolean.opBoolean","INTERSECT",EDGE,{"disambiguationData":[OD(0.0)],"derivedFrom":[makeQuery(id+"F5.opExtrude","SWEPT_FACE",FACE,{"disambiguationData":[OSD([sQuery(id+"F4.wireOp",EDGE,"E30")])]}),makeQuery(id+"F8.opExtrude","SWEPT_FACE",FACE,{"disambiguationData":[OSD([sQuery(id+"F7.wireOp",EDGE,"E67")])]})]});
            fillet(context, id + "F14", {"entities" : qUnion([Q0, Q1, Q2, Q3, Q4, Q5]), "radius" : 3 * mm, "tangentPropagation" : true, "allowEdgeOverflow" : false});
        }
        {
            var Q0;
            Q0=makeQuery(id+"F1.opExtrude","CAP_EDGE",EDGE,{"disambiguationData":[OSD([sQuery(id+"F0.wireOp",EDGE,"E1.bottom")])],"isStart":false});
            fillet(context, id + "F15", {"entities" : qUnion([Q0]), "radius" : 2 * mm, "tangentPropagation" : true, "allowEdgeOverflow" : false});
        }
        {
            var Q0;
            {var subQ0=sQuery(id+"F0.wireOp",EDGE,"E22.filletArc");var subQ1=sQuery(id+"F0.wireOp",EDGE,"E7");var subQ2=sQuery(id+"F0.wireOp",EDGE,"E6");var subQ3=sQuery(id+"F0.wireOp",EDGE,"E5");var subQ4=sQuery(id+"F0.wireOp",EDGE,"E4");var subQ5=sQuery(id+"F0.wireOp",EDGE,"E1.bottom");var subQ6=sQuery(id+"F0.wireOp",EDGE,"E21.filletArc");var subQ7=sQuery(id+"F0.wireOp",EDGE,"E1.top");var subQ8=sQuery(id+"F0.wireOp",EDGE,"E1.left");var subQ9=sQuery(id+"F0.wireOp",EDGE,"E1.right");var subQ10=sQuery(id+"F0.wireOp",EDGE,"E23.filletArc");var subQ11=sQuery(id+"F0.wireOp",EDGE,"E24.filletArc");Q0=makeQuery(id+"F2.boolean.opBoolean","SPLIT",FACE,{"disambiguationData":[TD([makeQuery(id+"F1.opExtrude","SWEPT_FACE",FACE,{"disambiguationData":[OSD([subQ5])]})])],"derivedFrom":makeQuery(id+"F1.opExtrude","CAP_FACE",FACE,{"disambiguationData":[OSD([subQ5,subQ7,subQ8,subQ9,subQ4,subQ3,subQ2,subQ1,subQ6,subQ0,subQ10,subQ11])],"isStart":true})});}
            var sketch = newSketch(context, id + "F16", { "sketchPlane" : qUnion([Q0])});
            skLineSegment(sketch, "E79", {"start": v(94.05, 208.38) * mm, "end": v(94.05, 238.38) * mm, "construction": true});
            skPoint(sketch, "E79.endSnap0", {"position": v(94.05, 185.88) * mm});
            skCircle(sketch, "E80", {"center": v(94.05, 238.38) * mm, "radius": 6 * mm});
            skArc(sketch, "E81", {"start": v(109.05, 238.38) * mm, "mid": v(94.05, 253.38) * mm, "end": v(79.05, 238.38) * mm});
            skLineSegment(sketch, "E82", {"start": v(109.05, 238.38) * mm, "end": v(109.05, 220.38) * mm});
            skLineSegment(sketch, "E83", {"start": v(79.05, 238.38) * mm, "end": v(79.05, 220.38) * mm});
            skLineSegment(sketch, "E84", {"start": v(79.05, 220.38) * mm, "end": v(67.05, 208.38) * mm});
            skLineSegment(sketch, "E85", {"start": v(109.05, 220.38) * mm, "end": v(121.05, 208.38) * mm});
            skLineSegment(sketch, "E86", {"start": v(14.05, 118.38) * mm, "end": v(174.05, 118.38) * mm, "construction": true});
            skLineSegment(sketch, "E87.MirrorCS", {"start": v(94.05, 28.38) * mm, "end": v(94.05, -1.62) * mm, "construction": true});
            skCircle(sketch, "E88.MirrorC", {"center": v(94.05, -1.62) * mm, "radius": 6 * mm});
            skArc(sketch, "E89.MirrorCS", {"start": v(109.05, -1.62) * mm, "mid": v(94.05, -16.62) * mm, "end": v(79.05, -1.62) * mm});
            skLineSegment(sketch, "E90.MirrorCS", {"start": v(109.05, -1.62) * mm, "end": v(109.05, 16.38) * mm});
            skLineSegment(sketch, "E91.MirrorCS", {"start": v(79.05, -1.62) * mm, "end": v(79.05, 16.38) * mm});
            skLineSegment(sketch, "E92.MirrorCS", {"start": v(79.05, 16.38) * mm, "end": v(67.05, 28.38) * mm});
            skLineSegment(sketch, "E93.MirrorCS", {"start": v(109.05, 16.38) * mm, "end": v(121.05, 28.38) * mm});
            skSolve(sketch);
        }
        {
            var Q0;
            Q0=makeQuery(id+"F16.imprint","IMPRINT",FACE,{"disambiguationData":[TD([[makeQuery(id+"F16.imprint","IMPRINT",EDGE,{"derivedFrom":sQuery(id+"F16.wireOp",EDGE,"E80")}),-1.0]])]});
            var Q1;
            Q1=makeQuery(id+"F16.imprint","IMPRINT",FACE,{"disambiguationData":[TD([[makeQuery(id+"F16.imprint","IMPRINT",EDGE,{"derivedFrom":sQuery(id+"F16.wireOp",EDGE,"E88.MirrorC")}),1.0]])]});
            var Q2;
            Q2=makeQuery(id+"F16.imprint","IMPRINT",FACE,{"disambiguationData":[TD([[makeQuery(id+"F16.imprint","IMPRINT",EDGE,{"derivedFrom":makeQuery(id+"F1.opExtrude","CAP_EDGE",EDGE,{"disambiguationData":[OSD([sQuery(id+"F0.wireOp",EDGE,"E1.left")])],"isStart":true})}),-1.0]])]});
            var Q3;
            Q3=makeQuery(id+"F2.opExtrude","CAP_FACE",FACE,{"disambiguationData":[OSD([sQuery(id+"F0.wireOp",EDGE,"E12"),sQuery(id+"F0.wireOp",EDGE,"E13"),sQuery(id+"F0.wireOp",EDGE,"E14"),sQuery(id+"F0.wireOp",EDGE,"E15"),sQuery(id+"F0.wireOp",EDGE,"E17.filletArc"),sQuery(id+"F0.wireOp",EDGE,"E18.filletArc"),sQuery(id+"F0.wireOp",EDGE,"E19.filletArc"),sQuery(id+"F0.wireOp",EDGE,"E20.filletArc"),sQuery(id+"F0.wireOp",EDGE,"E25.0"),sQuery(id+"F0.wireOp",EDGE,"E25.1"),sQuery(id+"F0.wireOp",EDGE,"E25.2"),sQuery(id+"F0.wireOp",EDGE,"E25.3"),sQuery(id+"F0.wireOp",EDGE,"E25.4"),sQuery(id+"F0.wireOp",EDGE,"E25.5"),sQuery(id+"F0.wireOp",EDGE,"E25.6"),sQuery(id+"F0.wireOp",EDGE,"E25.7")])],"isStart":false});
            extrude(context, id + "F17", {"entities" : qUnion([Q0, Q1, Q2]), "endBound" : BoundingType.UP_TO_SURFACE, "endBoundEntityFace" : qUnion([Q3]), "depth" : 25 * mm});
        }
    });
